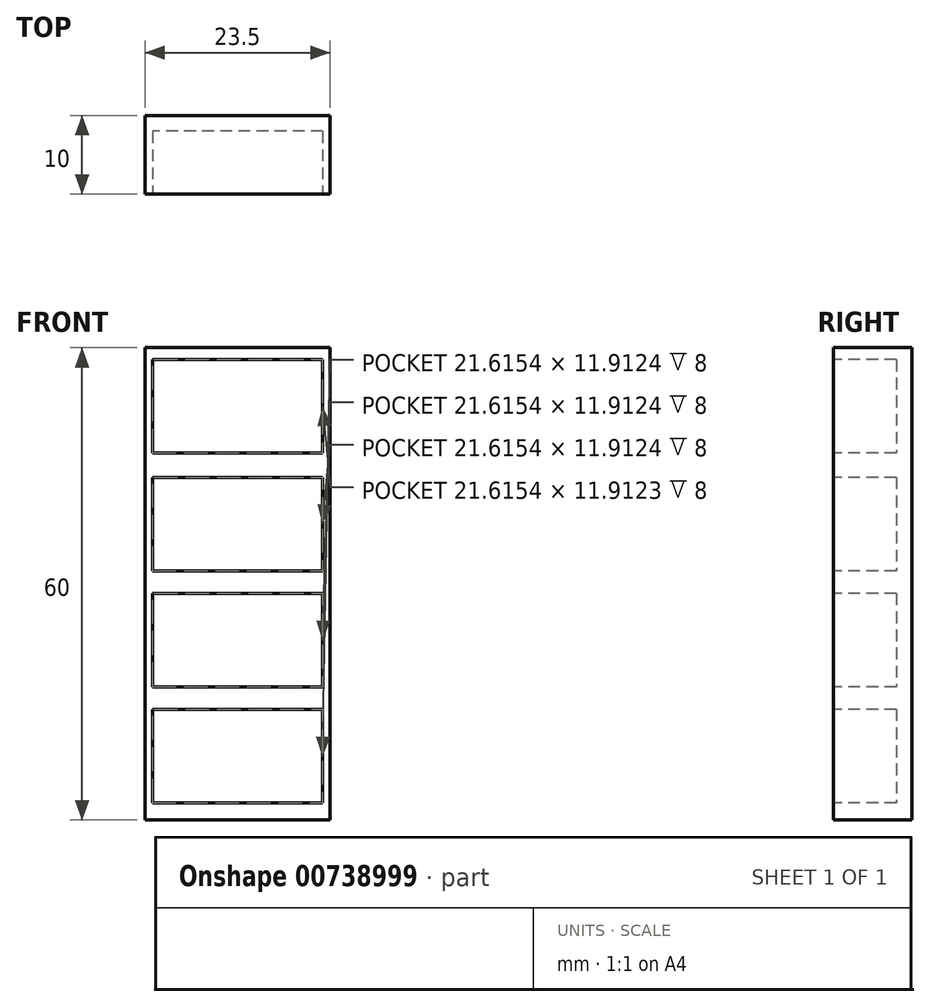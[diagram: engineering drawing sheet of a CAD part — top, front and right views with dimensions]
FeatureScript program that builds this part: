
annotation { "Feature Type Name" : "Feature", "Feature Type Description" : "" }
export const myFeature = defineFeature(function(context is Context, id is Id, definition is map)
    precondition{}
    {
        {
            var Q0;
            Q0=qCreatedBy(makeId("Top.planeOp"),FACE);
            var sketch = newSketch(context, id + "F0", { "sketchPlane" : qUnion([Q0])});
            skLineSegment(sketch, "E0.bottom", {"start": v(11.75, 5) * mm, "end": v(-11.75, 5) * mm});
            skLineSegment(sketch, "E0.top", {"start": v(11.75, -5) * mm, "end": v(-11.75, -5) * mm});
            skLineSegment(sketch, "E0.left", {"start": v(11.75, 5) * mm, "end": v(11.75, -5) * mm});
            skLineSegment(sketch, "E0.right", {"start": v(-11.75, 5) * mm, "end": v(-11.75, -5) * mm});
            skPoint(sketch, "E0.middle", {"position": v(0, 0) * mm});
            skSolve(sketch);
        }
        {
            var Q0;
            Q0 = qSketchRegion(id + "F0", true);
            extrude(context, id + "F1", {"entities" : qUnion([Q0]), "depth" : 60 * mm, "offsetDistance" : 25 * mm});
        }
        {
            var Q0;
            Q0=makeQuery(id+"F1.opExtrude","SWEPT_FACE",FACE,{"disambiguationData":[OSD([sQuery(id+"F0.wireOp",EDGE,"E0.top")])]});
            var sketch = newSketch(context, id + "F2", { "sketchPlane" : qUnion([Q0])});
            skLineSegment(sketch, "E1", {"start": v(0, 60) * mm, "end": v(0, 0) * mm, "construction": true});
            skLineSegment(sketch, "E2.bottom", {"start": v(10.8, 58.5) * mm, "end": v(-10.8, 58.5) * mm});
            skLineSegment(sketch, "E2.top", {"start": v(10.8, 46.6) * mm, "end": v(-10.8, 46.6) * mm});
            skLineSegment(sketch, "E2.left", {"start": v(10.8, 58.5) * mm, "end": v(10.8, 46.6) * mm});
            skLineSegment(sketch, "E2.right", {"start": v(-10.8, 58.5) * mm, "end": v(-10.8, 46.6) * mm});
            skPoint(sketch, "E2.middle", {"position": v(0, 52.55) * mm});
            skLineSegment(sketch, "E3.bottom", {"start": v(10.8, 43.53) * mm, "end": v(-10.8, 43.53) * mm});
            skLineSegment(sketch, "E3.top", {"start": v(10.8, 31.62) * mm, "end": v(-10.8, 31.62) * mm});
            skLineSegment(sketch, "E3.left", {"start": v(10.8, 43.53) * mm, "end": v(10.8, 31.62) * mm});
            skLineSegment(sketch, "E3.right", {"start": v(-10.8, 43.53) * mm, "end": v(-10.8, 31.62) * mm});
            skPoint(sketch, "E3.middle", {"position": v(0, 37.58) * mm});
            skLineSegment(sketch, "E4.bottom", {"start": v(10.8, 28.8) * mm, "end": v(-10.8, 28.8) * mm});
            skLineSegment(sketch, "E4.top", {"start": v(10.8, 16.88) * mm, "end": v(-10.8, 16.88) * mm});
            skLineSegment(sketch, "E4.left", {"start": v(10.8, 28.8) * mm, "end": v(10.8, 16.88) * mm});
            skLineSegment(sketch, "E4.right", {"start": v(-10.8, 28.8) * mm, "end": v(-10.8, 16.88) * mm});
            skPoint(sketch, "E4.middle", {"position": v(0, 22.84) * mm});
            skLineSegment(sketch, "E5.bottom", {"start": v(10.8, 14.06) * mm, "end": v(-10.8, 14.06) * mm});
            skLineSegment(sketch, "E5.top", {"start": v(10.8, 2.15) * mm, "end": v(-10.8, 2.15) * mm});
            skLineSegment(sketch, "E5.left", {"start": v(10.8, 14.06) * mm, "end": v(10.8, 2.15) * mm});
            skLineSegment(sketch, "E5.right", {"start": v(-10.8, 14.06) * mm, "end": v(-10.8, 2.15) * mm});
            skPoint(sketch, "E5.middle", {"position": v(0, 8.1) * mm});
            skSolve(sketch);
        }
        {
            var Q0;
            Q0 = qSketchRegion(id + "F2", true);
            extrude(context, id + "F3", {"entities" : qUnion([Q0]), "operationType" : NewBodyOperationType.REMOVE, "oppositeDirection" : true, "depth" : 8 * mm, "offsetDistance" : 25 * mm});
        }
    });
